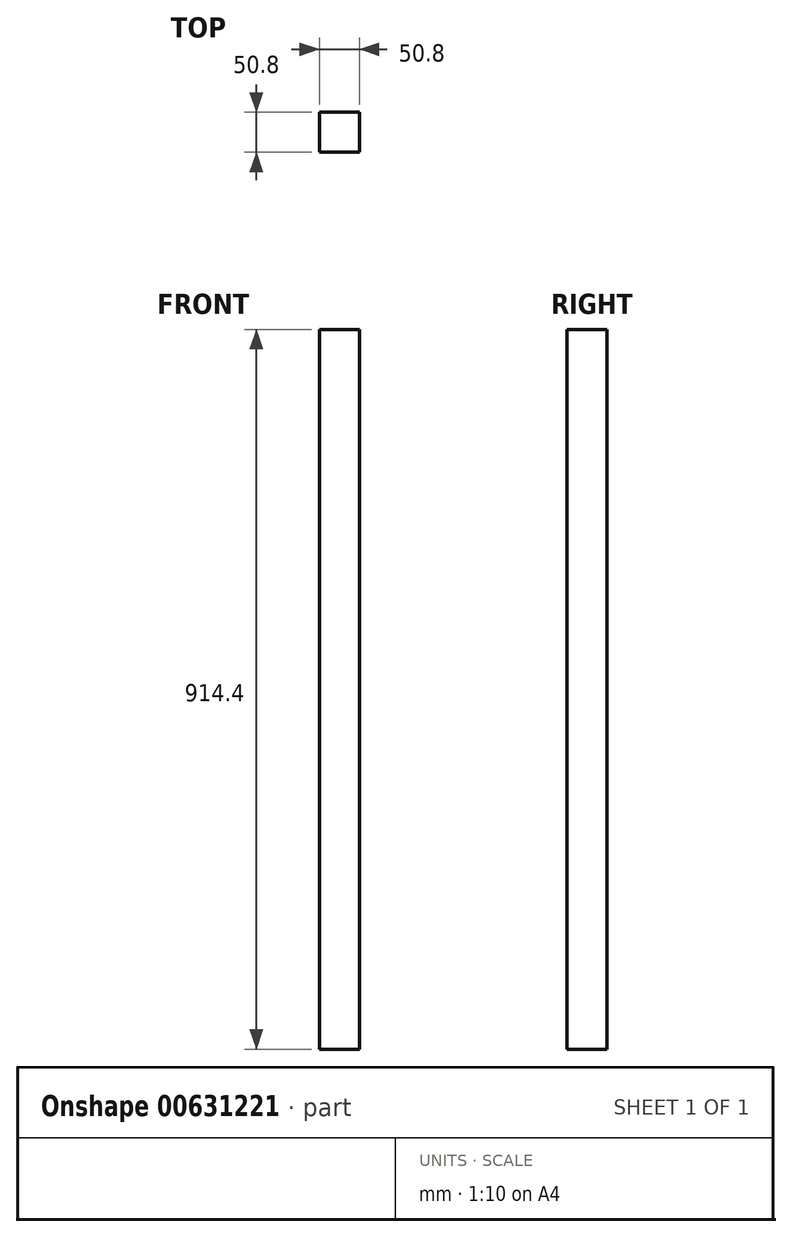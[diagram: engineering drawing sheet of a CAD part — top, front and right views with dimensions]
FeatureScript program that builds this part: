
annotation { "Feature Type Name" : "Feature", "Feature Type Description" : "" }
export const myFeature = defineFeature(function(context is Context, id is Id, definition is map)
    precondition{}
    {
        {
            var Q0;
            Q0=qCreatedBy(makeId("Top.planeOp"),FACE);
            var sketch = newSketch(context, id + "F0", { "sketchPlane" : qUnion([Q0])});
            skLineSegment(sketch, "E0.bottom", {"start": v(0, 0) * mm, "end": v(50.8, 0) * mm});
            skLineSegment(sketch, "E0.top", {"start": v(0, 50.8) * mm, "end": v(50.8, 50.8) * mm});
            skLineSegment(sketch, "E0.left", {"start": v(0, 0) * mm, "end": v(0, 50.8) * mm});
            skLineSegment(sketch, "E0.right", {"start": v(50.8, 0) * mm, "end": v(50.8, 50.8) * mm});
            skSolve(sketch);
        }
        {
            var Q0;
            Q0 = qSketchRegion(id + "F0", true);
            extrude(context, id + "F1", {"entities" : qUnion([Q0]), "depth" : 914.4 * mm, "offsetDistance" : 25.4 * mm});
        }
    });
